# Revit family: 1HVAC_Ductwork_Airzone_Return-Linear-Slat-Grille_RLQV
name_source: partatom
category: Air Terminals
revit_build: Autodesk Revit 2016 (Build: 20161004_0715(x64)
units: mm (PartAtom-declared; Revit-internal decimal feet)

## family parameters
Always vertical = Yes
Cut with Voids When Loaded = No
OmniClass Number = 23.75.70.21.27.11
OmniClass Title = Diffusers, Registers, and Grilles
Part Type = Normal
Room Calculation Point = Yes
Round Connector Dimension = Use Diameter
Shared = No
Work Plane-Based = No

## types (1)
- INVALID TYPE - Use Load Family and Type Catalog instead
    Accessories Material = Metal - AIRZONE - Extruded Aluminium - Anodized (Matt Silver Color)
    Ak = 2.8
    Ak1000 = 10
    Akn = 2.8
    Compatible Accesories = Mounting frame. Manual flow regulation. Plenum for grille (PREJ, FR-X2F). Grille deflector
    Damper Length = 40 mm
    Description = Grille of linear slats fixed at 15º
    Disclaimer = All information provided in this model is reviewed before being published. However, Airzone cannot guarantee this model is error-free, therefore users are strongly encouraged to check for technical documentation and updates
    Duct Height = 200 mm
    Duct Width = 300 mm
    Effective Area = 280.00 cm²
    Finish = White (RAL 9010)
    Fixing = Clip (K), mounting frame required. Screw (T), mounting frame required.
    Grille Left Offset = 10 mm
    Grille Material = Metal - AIRZONE - Grille 12.5 mm - White (RAL 9010)
    Grille Right Offset = 10 mm
    Left Cap Offset = 16 mm
    Long Description = Extruded aluminum supply grilles to enable the air flow supply. 26-mm standard frame. Horizontal slats fixed at 15º, positioned to a single direction with a second vertical moving deflection.
    Main Material = Metal - AIRZONE - Extruded Aluminium - White (RAL 9010)
    Manufacturer = AIRZONE
    Max Flow = 1500 m³/h
    Min Flow = 150 m³/h
    Model = INVALID – Type not loaded via type catalog
    Open Left End = No
    Open Right End = No
    Product Code = INVALID – Type not loaded via type catalog
    Product Comments = Refer to technical documentation for further details
    Product Documentation Download URL = http://doc.airzone.es
    Revit Model Version = 1.0
    Right Cap Offset = 16 mm
    Type Image Comments = Image available in product documentation download
    URL = www.airzone.es
    c1 = 0.000333
    c2 = -1.797
    c3 = -75.88
    c4 = -58
    c5 = 42.72
    c6 = 8.344
    c7 = 0.04784
    c8 = -0.5949

## geometry (parser evidence)
native form markers: Sweep x2
no freeform markers — native parametric forms only
